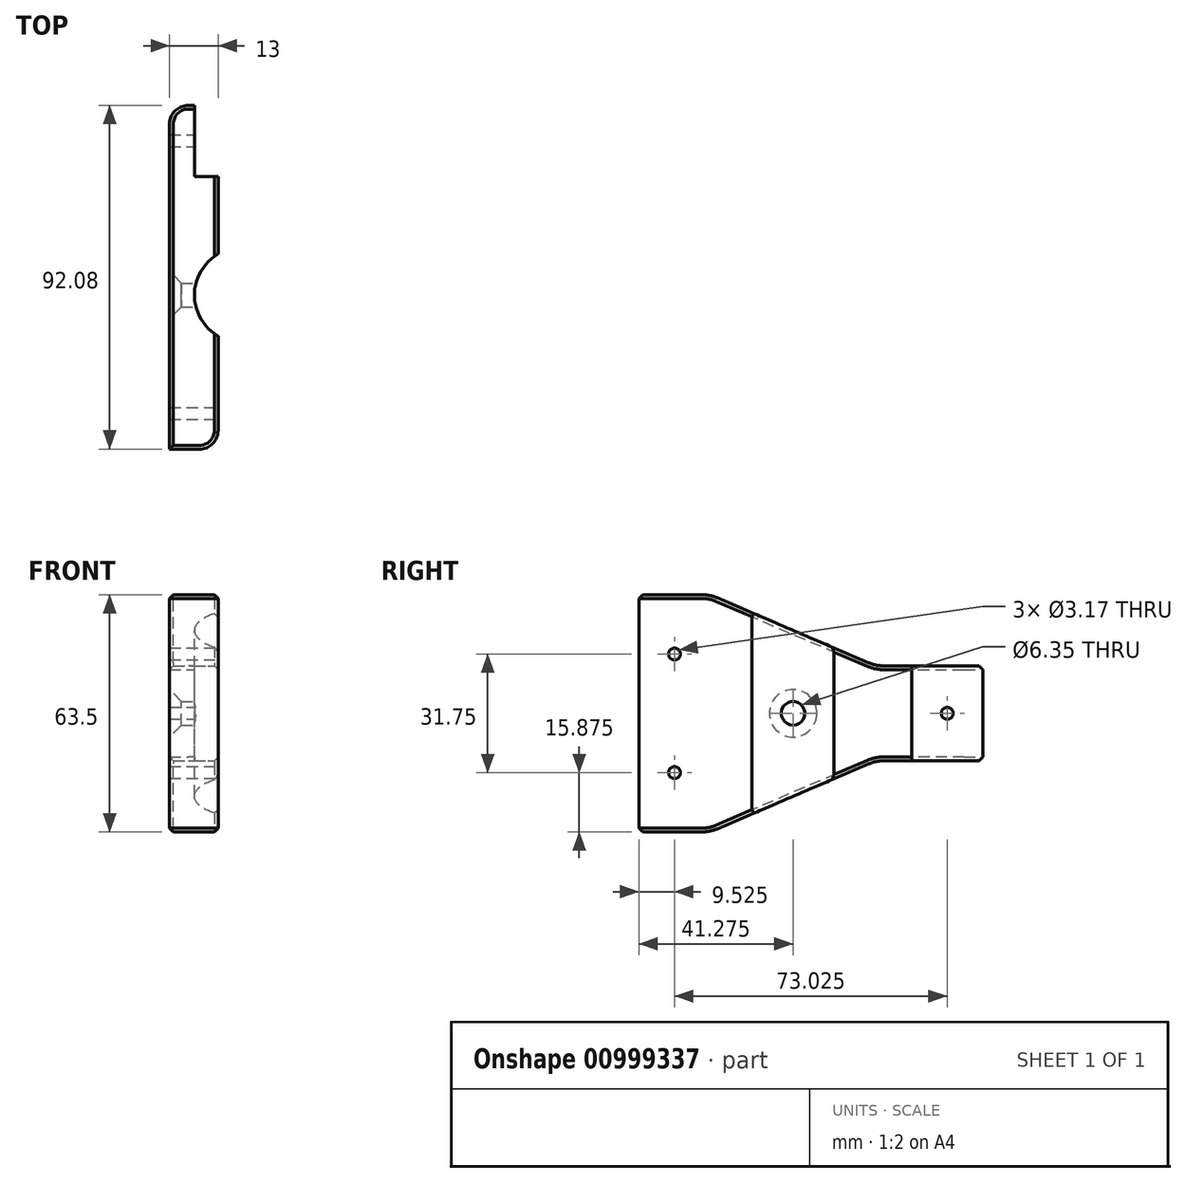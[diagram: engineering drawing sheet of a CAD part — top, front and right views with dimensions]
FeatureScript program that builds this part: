
annotation { "Feature Type Name" : "Feature", "Feature Type Description" : "" }
export const myFeature = defineFeature(function(context is Context, id is Id, definition is map)
    precondition{}
    {
        {
            var Q0;
            Q0=qCreatedBy(makeId("Right.planeOp"),FACE);
            var sketch = newSketch(context, id + "F0", { "sketchPlane" : qUnion([Q0])});
            skLineSegment(sketch, "E0", {"start": v(0, 0) * mm, "end": v(0, -31.75) * mm});
            skLineSegment(sketch, "E1", {"start": v(0, -31.75) * mm, "end": v(19.05, -31.75) * mm});
            skLineSegment(sketch, "E2", {"start": v(19.05, -31.75) * mm, "end": v(63.5, -12.7) * mm});
            skLineSegment(sketch, "E3", {"start": v(63.5, -12.7) * mm, "end": v(92.08, -12.7) * mm});
            skLineSegment(sketch, "E4", {"start": v(92.08, -12.7) * mm, "end": v(92.08, 0) * mm});
            skLineSegment(sketch, "E5.MirrorCS", {"start": v(0, 0) * mm, "end": v(0, 31.75) * mm});
            skLineSegment(sketch, "E6.MirrorCS", {"start": v(63.5, 12.7) * mm, "end": v(92.08, 12.7) * mm});
            skLineSegment(sketch, "E7.MirrorCS", {"start": v(0, 31.75) * mm, "end": v(19.05, 31.75) * mm});
            skLineSegment(sketch, "E8.MirrorCS", {"start": v(92.08, 12.7) * mm, "end": v(92.08, 0) * mm});
            skLineSegment(sketch, "E9.MirrorCS", {"start": v(19.05, 31.75) * mm, "end": v(63.5, 12.7) * mm});
            skCircle(sketch, "E10", {"center": v(82.55, 0) * mm, "radius": 1.59 * mm});
            skCircle(sketch, "E11", {"center": v(9.53, -15.88) * mm, "radius": 1.59 * mm});
            skCircle(sketch, "E12.MirrorC", {"center": v(9.53, 15.88) * mm, "radius": 1.59 * mm});
            skCircle(sketch, "E13", {"center": v(41.27, 0) * mm, "radius": 3.18 * mm});
            skLineSegment(sketch, "E14", {"start": v(73.03, -12.7) * mm, "end": v(73.03, 12.7) * mm, "construction": true});
            skLineSegment(sketch, "E15", {"start": v(79.37, 57.33) * mm, "end": v(79.38, -64.63) * mm, "construction": true});
            skSolve(sketch);
        }
        {
            var Q0;
            Q0 = qSketchRegion(id + "F0", true);
            extrude(context, id + "F1", {"entities" : qUnion([Q0]), "oppositeDirection" : true, "depth" : 13 * mm, "offsetDistance" : 25 * mm});
        }
        {
            var Q0;
            Q0=qCreatedBy(makeId("Top.planeOp"),FACE);
            var sketch = newSketch(context, id + "F2", { "sketchPlane" : qUnion([Q0])});
            skArc(sketch, "E16", {"start": v(0, 52.27) * mm, "mid": v(-6.35, 41.27) * mm, "end": v(0, 30.28) * mm});
            skLineSegment(sketch, "E17", {"start": v(0, 30.28) * mm, "end": v(0, 52.27) * mm});
            skLineSegment(sketch, "E18.bottom", {"start": v(0, 92.08) * mm, "end": v(-6.35, 92.08) * mm});
            skLineSegment(sketch, "E18.top", {"start": v(0, 73.03) * mm, "end": v(-6.35, 73.03) * mm});
            skLineSegment(sketch, "E18.left", {"start": v(0, 92.08) * mm, "end": v(0, 73.03) * mm});
            skLineSegment(sketch, "E18.right", {"start": v(-6.35, 92.08) * mm, "end": v(-6.35, 73.03) * mm});
            skSolve(sketch);
        }
        {
            var Q0;
            Q0 = qSketchRegion(id + "F2", true);
            extrude(context, id + "F3", {"entities" : qUnion([Q0]), "operationType" : NewBodyOperationType.REMOVE, "endBound" : BoundingType.SYMMETRIC, "oppositeDirection" : true, "depth" : 75 * mm, "offsetDistance" : 25 * mm});
        }
        {
            var Q0;
            Q0=makeQuery(id+"F1.opExtrude","SWEPT_EDGE",EDGE,{"disambiguationData":[OSD([sQuery(id+"F0.wireOp",EDGE,"E7.MirrorCS"),sQuery(id+"F0.wireOp",EDGE,"E9.MirrorCS")])]});
            var Q1;
            Q1=makeQuery(id+"F1.opExtrude","SWEPT_EDGE",EDGE,{"disambiguationData":[OSD([sQuery(id+"F0.wireOp",EDGE,"E6.MirrorCS"),sQuery(id+"F0.wireOp",EDGE,"E9.MirrorCS")])]});
            var Q2;
            Q2=makeQuery(id+"F1.opExtrude","SWEPT_EDGE",EDGE,{"disambiguationData":[OSD([sQuery(id+"F0.wireOp",EDGE,"E2"),sQuery(id+"F0.wireOp",EDGE,"E3")])]});
            var Q3;
            Q3=makeQuery(id+"F1.opExtrude","SWEPT_EDGE",EDGE,{"disambiguationData":[OSD([sQuery(id+"F0.wireOp",EDGE,"E1"),sQuery(id+"F0.wireOp",EDGE,"E2")])]});
            fillet(context, id + "F4", {"entities" : qUnion([Q0, Q1, Q2, Q3]), "radius" : 10 * mm, "tangentPropagation" : true, "allowEdgeOverflow" : false});
        }
        {
            var Q0;
            Q0=makeQuery(id+"F1.opExtrude","CAP_EDGE",EDGE,{"disambiguationData":[OSD([sQuery(id+"F0.wireOp",EDGE,"E4"),sQuery(id+"F0.wireOp",EDGE,"E8.MirrorCS")])],"isStart":false});
            var Q1;
            Q1=makeQuery(id+"F1.opExtrude","CAP_EDGE",EDGE,{"disambiguationData":[OSD([sQuery(id+"F0.wireOp",EDGE,"E0"),sQuery(id+"F0.wireOp",EDGE,"E5.MirrorCS")])],"isStart":true});
            fillet(context, id + "F5", {"entities" : qUnion([Q0, Q1]), "radius" : 5 * mm, "tangentPropagation" : true, "allowEdgeOverflow" : false});
        }
        {
            var Q0;
            Q0=makeQuery(id+"F1.opExtrude","CAP_EDGE",EDGE,{"disambiguationData":[OSD([sQuery(id+"F0.wireOp",EDGE,"E6.MirrorCS")])],"isStart":false});
            var Q1;
            Q1=makeQuery(id+"F1.opExtrude","CAP_EDGE",EDGE,{"disambiguationData":[OSD([sQuery(id+"F0.wireOp",EDGE,"E7.MirrorCS")])],"isStart":true});
            var Q2;
            {var subQ0=sQuery(id+"F0.wireOp",EDGE,"E9.MirrorCS");var subQ1=sQuery(id+"F0.wireOp",EDGE,"E6.MirrorCS");Q2=makeQuery(id+"F3.boolean.opBoolean","SPLIT",EDGE,{"disambiguationData":[TD([makeQuery(id+"F1.opExtrude","SWEPT_FACE",FACE,{"disambiguationData":[OSD([subQ1])]})])],"derivedFrom":makeQuery(id+"F1.opExtrude","CAP_EDGE",EDGE,{"disambiguationData":[OSD([subQ0])],"isStart":true})});}
            var Q3;
            Q3=makeQuery(id+"F1.opExtrude","CAP_EDGE",EDGE,{"disambiguationData":[OSD([sQuery(id+"F0.wireOp",EDGE,"E3")])],"isStart":true});
            var Q4;
            {var subQ0=sQuery(id+"F0.wireOp",EDGE,"E2");var subQ1=sQuery(id+"F0.wireOp",EDGE,"E1");Q4=makeQuery(id+"F3.boolean.opBoolean","SPLIT",EDGE,{"disambiguationData":[TD([makeQuery(id+"F1.opExtrude","SWEPT_FACE",FACE,{"disambiguationData":[OSD([subQ1])]})])],"derivedFrom":makeQuery(id+"F1.opExtrude","CAP_EDGE",EDGE,{"disambiguationData":[OSD([subQ0])],"isStart":true})});}
            var Q5;
            Q5=makeQuery(id+"F1.opExtrude","CAP_EDGE",EDGE,{"disambiguationData":[OSD([sQuery(id+"F0.wireOp",EDGE,"E3")])],"isStart":false});
            chamfer(context, id + "F6", {"entities" : qUnion([Q0, Q1, Q2, Q3, Q4, Q5]), "width" : 1 * mm, "tangentPropagation" : true});
        }
        {
            var Q0;
            Q0=makeQuery(id+"F1.opExtrude","CAP_EDGE",EDGE,{"disambiguationData":[OSD([sQuery(id+"F0.wireOp",EDGE,"E13")])],"isStart":false});
            chamfer(context, id + "F7", {"entities" : qUnion([Q0]), "width" : 3.17 * mm, "tangentPropagation" : true});
        }
    });
